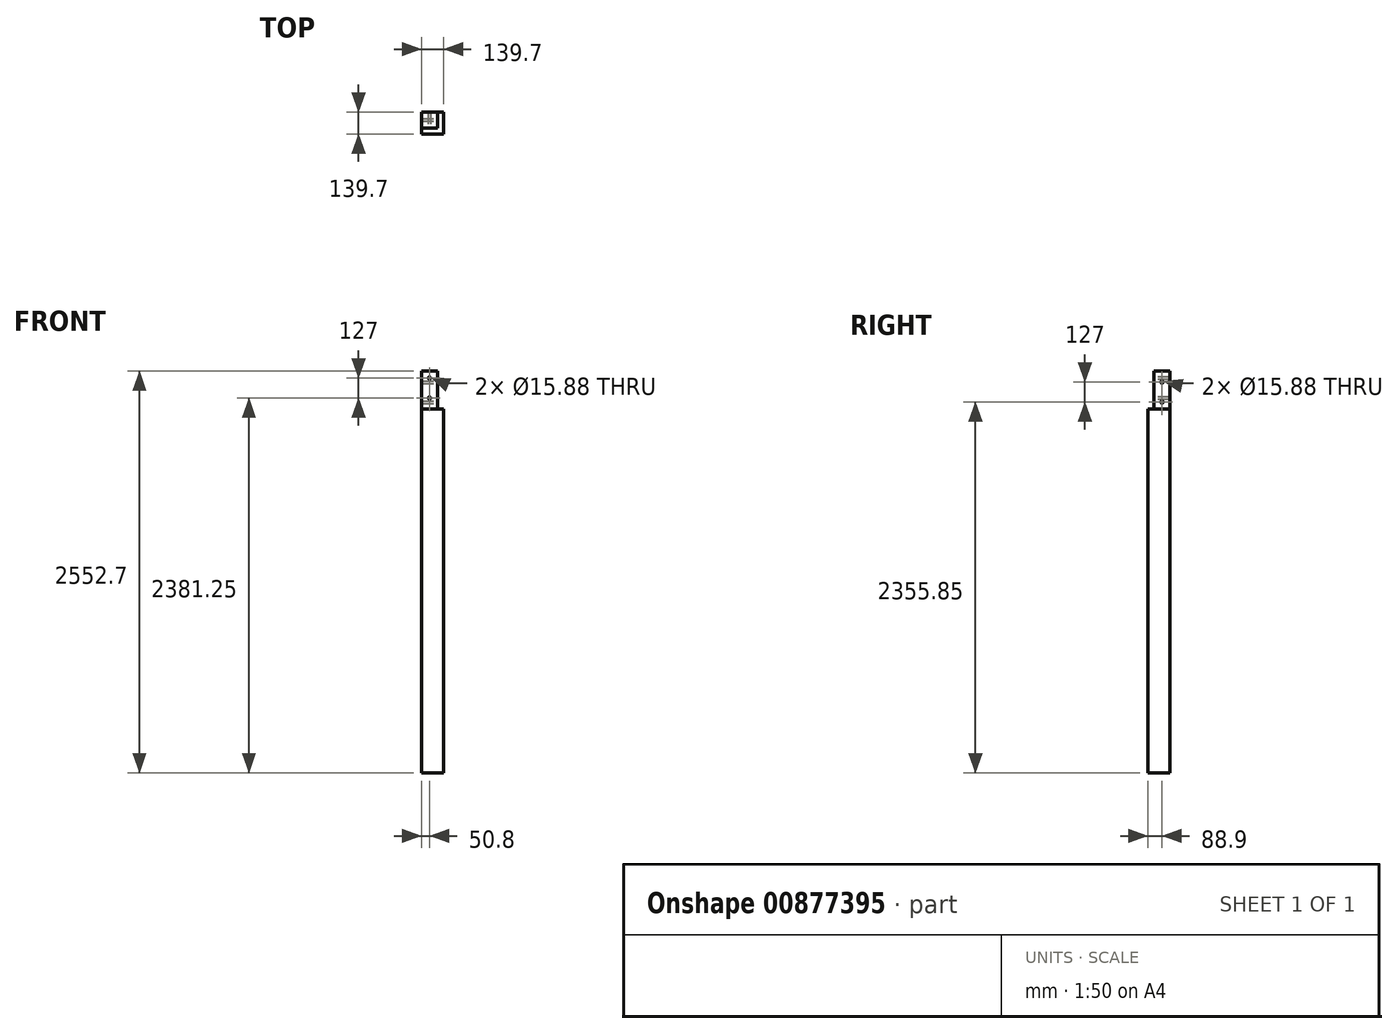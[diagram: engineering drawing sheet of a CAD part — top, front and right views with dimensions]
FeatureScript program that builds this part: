
annotation { "Feature Type Name" : "Feature", "Feature Type Description" : "" }
export const myFeature = defineFeature(function(context is Context, id is Id, definition is map)
    precondition{}
    {
        {
            var Q0;
            Q0=qCreatedBy(makeId("Top.planeOp"),FACE);
            var sketch = newSketch(context, id + "F0", { "sketchPlane" : qUnion([Q0])});
            skLineSegment(sketch, "E0.bottom", {"start": v(69.85, 69.85) * mm, "end": v(-69.85, 69.85) * mm});
            skLineSegment(sketch, "E0.top", {"start": v(69.85, -69.85) * mm, "end": v(-69.85, -69.85) * mm});
            skLineSegment(sketch, "E0.left", {"start": v(69.85, 69.85) * mm, "end": v(69.85, -69.85) * mm});
            skLineSegment(sketch, "E0.right", {"start": v(-69.85, 69.85) * mm, "end": v(-69.85, -69.85) * mm});
            skPoint(sketch, "E0.middle", {"position": v(0, 0) * mm});
            skSolve(sketch);
        }
        {
            var Q0;
            Q0=makeQuery(id+"F0.imprint","IMPRINT",FACE,{"disambiguationData":[TD([[makeQuery(id+"F0.imprint","IMPRINT",EDGE,{"derivedFrom":sQuery(id+"F0.wireOp",EDGE,"E0.bottom")}),1.0]])]});
            extrude(context, id + "F1", {"entities" : qUnion([Q0]), "oppositeDirection" : true, "depth" : 2552.7 * mm, "offsetDistance" : 25.4 * mm});
        }
        {
            var Q0;
            Q0=qCreatedBy(makeId("Front.planeOp"),FACE);
            var sketch = newSketch(context, id + "F2", { "sketchPlane" : qUnion([Q0])});
            skLineSegment(sketch, "E1.bottom", {"start": v(69.85, 0) * mm, "end": v(31.75, 0) * mm});
            skLineSegment(sketch, "E1.top", {"start": v(69.85, -241.3) * mm, "end": v(31.75, -241.3) * mm});
            skLineSegment(sketch, "E1.left", {"start": v(69.85, 0) * mm, "end": v(69.85, -241.3) * mm});
            skLineSegment(sketch, "E1.right", {"start": v(31.75, 0) * mm, "end": v(31.75, -241.3) * mm});
            skSolve(sketch);
        }
        {
            var Q0;
            Q0=qSketchRegion(id+"F2",true);
            extrude(context, id + "F3", {"entities" : qUnion([Q0]), "operationType" : NewBodyOperationType.REMOVE, "endBound" : BoundingType.THROUGH_ALL, "depth" : 25.4 * mm, "offsetDistance" : 25.4 * mm, "hasSecondDirection" : true, "secondDirectionBound" : SecondDirectionBoundingType.THROUGH_ALL, "secondDirectionOppositeDirection" : true, "secondDirectionDepth" : 25.4 * mm});
        }
        {
            var Q0;
            Q0=qCreatedBy(makeId("Right.planeOp"),FACE);
            var sketch = newSketch(context, id + "F4", { "sketchPlane" : qUnion([Q0])});
            skLineSegment(sketch, "E2.bottom", {"start": v(-69.85, 0) * mm, "end": v(-31.75, 0) * mm});
            skLineSegment(sketch, "E2.top", {"start": v(-69.85, -241.3) * mm, "end": v(-31.75, -241.3) * mm});
            skLineSegment(sketch, "E2.left", {"start": v(-69.85, 0) * mm, "end": v(-69.85, -241.3) * mm});
            skLineSegment(sketch, "E2.right", {"start": v(-31.75, 0) * mm, "end": v(-31.75, -241.3) * mm});
            skSolve(sketch);
        }
        {
            var Q0;
            Q0=qSketchRegion(id+"F4",true);
            extrude(context, id + "F5", {"entities" : qUnion([Q0]), "operationType" : NewBodyOperationType.REMOVE, "endBound" : BoundingType.THROUGH_ALL, "depth" : 25.4 * mm, "offsetDistance" : 25.4 * mm, "hasSecondDirection" : true, "secondDirectionBound" : SecondDirectionBoundingType.THROUGH_ALL, "secondDirectionOppositeDirection" : true, "secondDirectionDepth" : 25.4 * mm});
        }
        {
            var Q0;
            Q0=makeQuery(id+"F5.boolean.opBoolean","COPY",FACE,{"derivedFrom":makeQuery(id+"F5.opExtrude","SWEPT_FACE",FACE,{"disambiguationData":[OSD([sQuery(id+"F4.wireOp",EDGE,"E2.right")])]})});
            var sketch = newSketch(context, id + "F6", { "sketchPlane" : qUnion([Q0])});
            skLineSegment(sketch, "E3", {"start": v(-19.05, 0) * mm, "end": v(-19.05, -241.3) * mm, "construction": true});
            skLineSegment(sketch, "E4", {"start": v(-19.05, -44.45) * mm, "end": v(-19.05, -171.45) * mm});
            skPoint(sketch, "E5", {"position": v(-19.05, -107.95) * mm});
            skPoint(sketch, "E6", {"position": v(-19.05, -120.65) * mm});
            skSolve(sketch);
        }
        {
            var Q0;
            Q0=sQuery(id+"F6.wireOp",VERTEX,"E4.start");
            var Q1;
            Q1=sQuery(id+"F6.wireOp",VERTEX,"E4.end");
            var Q2;
            Q2=makeQuery(id+"F1.opExtrude","SWEPT_BODY",BODY,{"disambiguationData":[OSD([sQuery(id+"F0.wireOp",EDGE,"E0.bottom"),sQuery(id+"F0.wireOp",EDGE,"E0.top"),sQuery(id+"F0.wireOp",EDGE,"E0.left"),sQuery(id+"F0.wireOp",EDGE,"E0.right")])]});
            hole(context, id + "F7", {"style" : HoleStyle.SIMPLE, "endStyle" : HoleEndStyle.THROUGH, "holeDiameter" : 15.88 * mm, "majorDiameter" : 6.35 * mm, "isTappedThrough" : true, "tappedDepth" : 12.7 * mm, "tapClearance" : 3, "locations" : qUnion([Q0, Q1]), "scope" : qUnion([Q2])});
        }
        {
            var Q0;
            Q0=makeQuery(id+"F3.boolean.opBoolean","COPY",FACE,{"derivedFrom":makeQuery(id+"F3.opExtrude","SWEPT_FACE",FACE,{"disambiguationData":[OSD([sQuery(id+"F2.wireOp",EDGE,"E1.right")])]})});
            var sketch = newSketch(context, id + "F8", { "sketchPlane" : qUnion([Q0])});
            skLineSegment(sketch, "E7", {"start": v(19.05, 0) * mm, "end": v(19.05, -241.3) * mm, "construction": true});
            skLineSegment(sketch, "E8", {"start": v(19.05, -69.85) * mm, "end": v(19.05, -196.85) * mm});
            skPoint(sketch, "E9", {"position": v(19.05, -120.65) * mm});
            skPoint(sketch, "E10", {"position": v(19.05, -133.35) * mm});
            skSolve(sketch);
        }
        {
            var Q0;
            Q0=sQuery(id+"F8.wireOp",VERTEX,"E8.start");
            var Q1;
            Q1=sQuery(id+"F8.wireOp",VERTEX,"E8.end");
            var Q2;
            Q2=makeQuery(id+"F1.opExtrude","SWEPT_BODY",BODY,{"disambiguationData":[OSD([sQuery(id+"F0.wireOp",EDGE,"E0.bottom"),sQuery(id+"F0.wireOp",EDGE,"E0.top"),sQuery(id+"F0.wireOp",EDGE,"E0.left"),sQuery(id+"F0.wireOp",EDGE,"E0.right")])]});
            hole(context, id + "F9", {"style" : HoleStyle.SIMPLE, "endStyle" : HoleEndStyle.THROUGH, "holeDiameter" : 15.88 * mm, "majorDiameter" : 6.35 * mm, "isTappedThrough" : true, "tappedDepth" : 12.7 * mm, "tapClearance" : 3, "locations" : qUnion([Q0, Q1]), "scope" : qUnion([Q2])});
        }
    });
